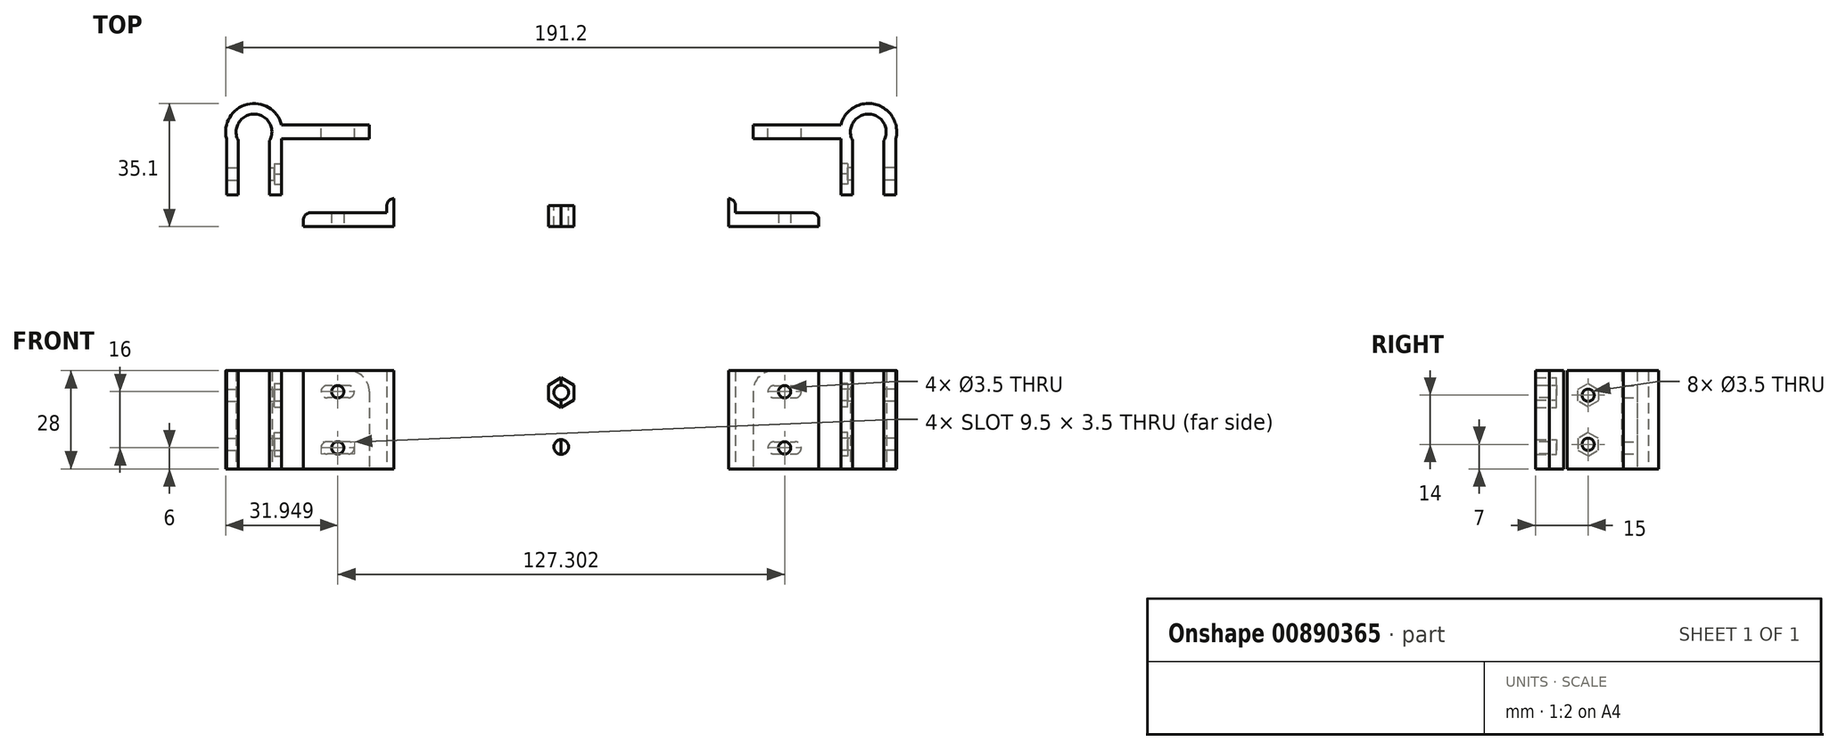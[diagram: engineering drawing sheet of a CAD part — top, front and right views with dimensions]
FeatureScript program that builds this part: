
annotation { "Feature Type Name" : "Feature", "Feature Type Description" : "" }
export const myFeature = defineFeature(function(context is Context, id is Id, definition is map)
    precondition{}
    {
        {
            var Q0;
            Q0=qCreatedBy(makeId("Top.planeOp"),FACE);
            var sketch = newSketch(context, id + "F0", { "sketchPlane" : qUnion([Q0])});
            skCircle(sketch, "E0", {"center": v(-87.5, 0) * mm, "radius": 5.1 * mm});
            skCircle(sketch, "E1", {"center": v(-87.5, 0) * mm, "radius": 8.1 * mm});
            skLineSegment(sketch, "E2.bottom", {"start": v(-95.35, -2) * mm, "end": v(-79.65, -2) * mm});
            skLineSegment(sketch, "E2.top", {"start": v(-95.35, -18) * mm, "end": v(-79.65, -18) * mm});
            skLineSegment(sketch, "E2.left", {"start": v(-95.35, -2) * mm, "end": v(-95.35, -18) * mm});
            skLineSegment(sketch, "E2.right", {"start": v(-79.65, -2) * mm, "end": v(-79.65, -18) * mm});
            skLineSegment(sketch, "E3.bottom", {"start": v(-91.95, -2.5) * mm, "end": v(-83.05, -2.5) * mm});
            skLineSegment(sketch, "E3.top", {"start": v(-91.95, -18) * mm, "end": v(-83.05, -18) * mm});
            skLineSegment(sketch, "E3.left", {"start": v(-91.95, -2.5) * mm, "end": v(-91.95, -18) * mm});
            skLineSegment(sketch, "E3.right", {"start": v(-83.05, -2.5) * mm, "end": v(-83.05, -18) * mm});
            skLineSegment(sketch, "E4.bottom", {"start": v(-79.65, 2) * mm, "end": v(-54.65, 2) * mm});
            skLineSegment(sketch, "E4.top", {"start": v(-79.65, -2) * mm, "end": v(-54.65, -2) * mm});
            skLineSegment(sketch, "E4.left", {"start": v(-79.65, 2) * mm, "end": v(-79.65, -2) * mm});
            skLineSegment(sketch, "E4.right", {"start": v(-54.65, 2) * mm, "end": v(-54.65, -2) * mm});
            skPoint(sketch, "E5", {"position": v(-54.65, 0) * mm});
            skSolve(sketch);
        }
        {
            var Q0;
            {var subQ0=sQuery(id+"F0.wireOp",EDGE,"E2.left");Q0=makeQuery(id+"F0.imprint","IMPRINT",FACE,{"disambiguationData":[TD([[makeQuery(id+"F0.imprint","IMPRINT",EDGE,{"derivedFrom":subQ0}),1.0]])]});}
            var Q1;
            {var subQ0=sQuery(id+"F0.wireOp",EDGE,"E2.bottom");var subQ1=sQuery(id+"F0.wireOp",EDGE,"E0");var subQ2=makeQuery(id+"F0.imprint","INTERSECT",VERTEX,{"disambiguationData":[OD(0.0)],"derivedFrom":[subQ1,subQ0]});Q1=makeQuery(id+"F0.imprint","IMPRINT",FACE,{"disambiguationData":[TD([[makeQuery(id+"F0.imprint","IMPRINT",EDGE,{"disambiguationData":[TD([[subQ2,-1.0]])],"derivedFrom":subQ1}),-1.0]])]});}
            var Q2;
            {var subQ0=sQuery(id+"F0.wireOp",EDGE,"E4.left");Q2=makeQuery(id+"F0.imprint","IMPRINT",FACE,{"disambiguationData":[TD([[makeQuery(id+"F0.imprint","IMPRINT",EDGE,{"derivedFrom":subQ0}),-1.0]])]});}
            var Q3;
            {var subQ0=sQuery(id+"F0.wireOp",EDGE,"E2.right");Q3=makeQuery(id+"F0.imprint","IMPRINT",FACE,{"disambiguationData":[TD([[makeQuery(id+"F0.imprint","IMPRINT",EDGE,{"derivedFrom":subQ0}),-1.0]])]});}
            var Q4;
            {var subQ1=sQuery(id+"F0.wireOp",EDGE,"E0");var subQ3=sQuery(id+"F0.wireOp",EDGE,"E2.bottom");var subQ4=makeQuery(id+"F0.imprint","INTERSECT",VERTEX,{"disambiguationData":[OD(1.0)],"derivedFrom":[subQ1,subQ3]});Q4=makeQuery(id+"F0.imprint","IMPRINT",FACE,{"disambiguationData":[TD([[makeQuery(id+"F0.imprint","IMPRINT",EDGE,{"disambiguationData":[TD([[subQ4,1.0]])],"derivedFrom":subQ1}),-1.0]])]});}
            var Q5;
            {var subQ0=sQuery(id+"F0.wireOp",EDGE,"E4.bottom");Q5=makeQuery(id+"F0.imprint","IMPRINT",FACE,{"disambiguationData":[TD([[makeQuery(id+"F0.imprint","IMPRINT",EDGE,{"derivedFrom":subQ0}),-1.0]])]});}
            var Q6;
            {var subQ0=sQuery(id+"F0.wireOp",EDGE,"E4.left");Q6=makeQuery(id+"F0.imprint","IMPRINT",FACE,{"disambiguationData":[TD([[makeQuery(id+"F0.imprint","IMPRINT",EDGE,{"derivedFrom":subQ0}),1.0]])]});}
            extrude(context, id + "F1", {"entities" : qUnion([Q0, Q1, Q2, Q3, Q4, Q5, Q6]), "depth" : 28 * mm, "offsetDistance" : 25 * mm});
        }
        {
            var Q0;
            Q0=makeQuery(id+"F1.opExtrude","SWEPT_FACE",FACE,{"disambiguationData":[OSD([sQuery(id+"F0.wireOp",EDGE,"E2.right")])]});
            var sketch = newSketch(context, id + "F2", { "sketchPlane" : qUnion([Q0])});
            skCircle(sketch, "E6", {"center": v(-12, 21) * mm, "radius": 1.75 * mm});
            skLineSegment(sketch, "E7", {"start": v(-2, 14) * mm, "end": v(-18, 14) * mm, "construction": true});
            skCircle(sketch, "E8.MirrorC", {"center": v(-12, 7) * mm, "radius": 1.75 * mm});
            skCircle(sketch, "E9.cCircle", {"center": v(-12, 21) * mm, "radius": 2.9 * mm, "construction": true});
            skLineSegment(sketch, "E9.0", {"start": v(-12, 17.65) * mm, "end": v(-14.9, 19.33) * mm});
            skLineSegment(sketch, "E9.1", {"start": v(-14.9, 19.33) * mm, "end": v(-14.9, 22.67) * mm});
            skLineSegment(sketch, "E9.2", {"start": v(-14.9, 22.67) * mm, "end": v(-12, 24.35) * mm});
            skLineSegment(sketch, "E9.3", {"start": v(-12, 24.35) * mm, "end": v(-9.1, 22.67) * mm});
            skLineSegment(sketch, "E9.4", {"start": v(-9.1, 22.67) * mm, "end": v(-9.1, 19.33) * mm});
            skLineSegment(sketch, "E9.5", {"start": v(-9.1, 19.33) * mm, "end": v(-12, 17.65) * mm});
            skPoint(sketch, "E9.0.midPoint", {"position": v(-13.45, 18.49) * mm});
            skLineSegment(sketch, "E10.MirrorCS", {"start": v(-12, 10.35) * mm, "end": v(-14.9, 8.67) * mm});
            skLineSegment(sketch, "E11.MirrorCS", {"start": v(-9.1, 8.67) * mm, "end": v(-12, 10.35) * mm});
            skLineSegment(sketch, "E12.MirrorCS", {"start": v(-9.1, 5.33) * mm, "end": v(-9.1, 8.67) * mm});
            skLineSegment(sketch, "E13.MirrorCS", {"start": v(-12, 3.65) * mm, "end": v(-9.1, 5.33) * mm});
            skLineSegment(sketch, "E14.MirrorCS", {"start": v(-14.9, 5.33) * mm, "end": v(-12, 3.65) * mm});
            skLineSegment(sketch, "E15.MirrorCS", {"start": v(-14.9, 8.67) * mm, "end": v(-14.9, 5.33) * mm});
            skSolve(sketch);
        }
        {
            var Q0;
            Q0=makeQuery(id+"F1.opExtrude","SWEPT_FACE",FACE,{"disambiguationData":[OSD([sQuery(id+"F0.wireOp",EDGE,"E4.bottom")])]});
            var sketch = newSketch(context, id + "F3", { "sketchPlane" : qUnion([Q0])});
            skLineSegment(sketch, "E16", {"start": v(54.65, 14) * mm, "end": v(79.65, 14) * mm, "construction": true});
            skLineSegment(sketch, "E17", {"start": v(60.65, 22) * mm, "end": v(66.65, 22) * mm, "construction": true});
            skArc(sketch, "E18.0.startCap", {"start": v(60.65, 20.25) * mm, "mid": v(58.9, 22) * mm, "end": v(60.65, 23.75) * mm});
            skArc(sketch, "E18.0.endCap", {"start": v(66.65, 23.75) * mm, "mid": v(68.4, 22) * mm, "end": v(66.65, 20.25) * mm});
            skLineSegment(sketch, "E18.0.left", {"start": v(60.65, 23.75) * mm, "end": v(66.65, 23.75) * mm});
            skLineSegment(sketch, "E18.0.right", {"start": v(60.65, 20.25) * mm, "end": v(66.65, 20.25) * mm});
            skLineSegment(sketch, "E19.MirrorCS", {"start": v(60.65, 4.25) * mm, "end": v(66.65, 4.25) * mm});
            skArc(sketch, "E20.MirrorCS", {"start": v(66.65, 4.25) * mm, "mid": v(68.4, 6) * mm, "end": v(66.65, 7.75) * mm});
            skLineSegment(sketch, "E21.MirrorCS", {"start": v(60.65, 6) * mm, "end": v(66.65, 6) * mm, "construction": true});
            skLineSegment(sketch, "E22.MirrorCS", {"start": v(60.65, 7.75) * mm, "end": v(66.65, 7.75) * mm});
            skArc(sketch, "E23.MirrorCS", {"start": v(60.65, 7.75) * mm, "mid": v(58.9, 6) * mm, "end": v(60.65, 4.25) * mm});
            skSolve(sketch);
        }
        {
            var Q0;
            Q0 = qSketchRegion(id + "F2", true);
            extrude(context, id + "F4", {"entities" : qUnion([Q0]), "operationType" : NewBodyOperationType.REMOVE, "oppositeDirection" : true, "depth" : 2 * mm, "offsetDistance" : 25 * mm});
        }
        {
            var Q0;
            Q0=makeQuery(id+"F4.boolean.opBoolean","SPLIT",FACE,{"disambiguationData":[TD([makeQuery(id+"F4.opExtrude","SWEPT_FACE",FACE,{"disambiguationData":[OSD([sQuery(id+"F2.wireOp",EDGE,"E6")])]})])],"derivedFrom":makeQuery(id+"F1.opExtrude","SWEPT_FACE",FACE,{"disambiguationData":[OSD([sQuery(id+"F0.wireOp",EDGE,"E2.right")])]})});
            var Q1;
            Q1=makeQuery(id+"F4.boolean.opBoolean","SPLIT",FACE,{"disambiguationData":[TD([makeQuery(id+"F4.opExtrude","SWEPT_FACE",FACE,{"disambiguationData":[OSD([sQuery(id+"F2.wireOp",EDGE,"E8.MirrorC")])]})])],"derivedFrom":makeQuery(id+"F1.opExtrude","SWEPT_FACE",FACE,{"disambiguationData":[OSD([sQuery(id+"F0.wireOp",EDGE,"E2.right")])]})});
            extrude(context, id + "F5", {"entities" : qUnion([Q0, Q1]), "operationType" : NewBodyOperationType.REMOVE, "oppositeDirection" : true, "depth" : 25 * mm, "offsetDistance" : 25 * mm});
        }
        {
            var Q0;
            Q0 = qSketchRegion(id + "F3", true);
            extrude(context, id + "F6", {"entities" : qUnion([Q0]), "operationType" : NewBodyOperationType.REMOVE, "oppositeDirection" : true, "depth" : 25 * mm, "offsetDistance" : 25 * mm});
        }
        {
            var Q0;
            Q0=makeQuery(id+"F1.opExtrude","CAP_EDGE",EDGE,{"disambiguationData":[OSD([sQuery(id+"F0.wireOp",EDGE,"E4.right")])],"isStart":false});
            fillet(context, id + "F7", {"entities" : qUnion([Q0]), "tangentPropagation" : true, "radius" : 6 * mm, "defaultsChanged" : true, "vertexSettings" : [], "allowEdgeOverflow" : false});
        }
        {
            var Q0;
            Q0=makeQuery(id+"F1.opExtrude","SWEPT_BODY",BODY,{"disambiguationData":[OSD([sQuery(id+"F0.wireOp",EDGE,"E0"),sQuery(id+"F0.wireOp",EDGE,"E1"),sQuery(id+"F0.wireOp",EDGE,"E2.top"),sQuery(id+"F0.wireOp",EDGE,"E2.left"),sQuery(id+"F0.wireOp",EDGE,"E2.right"),sQuery(id+"F0.wireOp",EDGE,"E3.left"),sQuery(id+"F0.wireOp",EDGE,"E3.right"),sQuery(id+"F0.wireOp",EDGE,"E4.bottom"),sQuery(id+"F0.wireOp",EDGE,"E4.top"),sQuery(id+"F0.wireOp",EDGE,"E4.right")])]});
            var Q1;
            Q1=qCreatedBy(makeId("Right.planeOp"),FACE);
            mirror(context, id + "F8", {"entities" : qUnion([Q0]), "mirrorPlane" : qUnion([Q1])});
        }
        {
            var Q0;
            Q0=makeQuery(id+"F1.opExtrude","SWEPT_FACE",FACE,{"disambiguationData":[OSD([sQuery(id+"F0.wireOp",EDGE,"E4.top")])]});
            cPlane(context, id + "F9", {"entities" : qUnion([Q0]), "cplaneType" : CPlaneType.OFFSET, "offset" : 25 * mm, "width" : 150 * mm, "height" : 150 * mm});
        }
        {
            var Q0;
            Q0=qCreatedBy(id+"F9.planeOp",FACE);
            var sketch = newSketch(context, id + "F10", { "sketchPlane" : qUnion([Q0])});
            skLineSegment(sketch, "E24.bottom", {"start": v(-73.4, 28) * mm, "end": v(0, 28) * mm});
            skLineSegment(sketch, "E24.top", {"start": v(-73.4, 0) * mm, "end": v(0, 0) * mm});
            skLineSegment(sketch, "E24.left", {"start": v(-73.4, 28) * mm, "end": v(-73.4, 0) * mm});
            skLineSegment(sketch, "E24.right", {"start": v(0, 28) * mm, "end": v(0, 0) * mm});
            skCircle(sketch, "E25", {"center": v(-63.65, 22) * mm, "radius": 1.75 * mm});
            skLineSegment(sketch, "E26", {"start": v(-73.4, 14) * mm, "end": v(0, 14) * mm, "construction": true});
            skLineSegment(sketch, "E27", {"start": v(-63.65, 23.75) * mm, "end": v(-63.65, 20.25) * mm, "construction": true});
            skCircle(sketch, "E28.MirrorC", {"center": v(-63.65, 6) * mm, "radius": 1.75 * mm});
            skLineSegment(sketch, "E29", {"start": v(-49.65, 28) * mm, "end": v(-49.65, 0) * mm});
            skSolve(sketch);
        }
        {
            var Q0;
            {var subQ0=sQuery(id+"F10.wireOp",EDGE,"E24.left");Q0=makeQuery(id+"F10.imprint","IMPRINT",FACE,{"disambiguationData":[TD([[makeQuery(id+"F10.imprint","IMPRINT",EDGE,{"derivedFrom":subQ0}),1.0]])]});}
            extrude(context, id + "F11", {"entities" : qUnion([Q0]), "oppositeDirection" : true, "depth" : 4 * mm, "offsetDistance" : 25 * mm});
        }
        {
            var Q0;
            {var subQ2=sQuery(id+"F10.wireOp",EDGE,"E24.right");Q0=makeQuery(id+"F10.imprint","IMPRINT",FACE,{"disambiguationData":[TD([[makeQuery(id+"F10.imprint","IMPRINT",EDGE,{"derivedFrom":subQ2}),-1.0]])]});}
            extrude(context, id + "F12", {"entities" : qUnion([Q0]), "operationType" : NewBodyOperationType.ADD, "oppositeDirection" : true, "depth" : 8 * mm, "offsetDistance" : 25 * mm});
        }
        {
            var Q0;
            Q0=makeQuery(id+"F11.opExtrude","CAP_EDGE",EDGE,{"disambiguationData":[OSD([sQuery(id+"F10.wireOp",EDGE,"E24.left")])],"isStart":false});
            var Q1;
            Q1=makeQuery(id+"F12.opExtrude","CAP_EDGE",EDGE,{"disambiguationData":[OSD([sQuery(id+"F10.wireOp",EDGE,"E29")])],"isStart":false});
            var Q2;
            Q2=makeQuery(id+"F11.opExtrude","CAP_EDGE",EDGE,{"disambiguationData":[OSD([sQuery(id+"F10.wireOp",EDGE,"E29")])],"isStart":false});
            fillet(context, id + "F13", {"entities" : qUnion([Q0, Q1, Q2]), "tangentPropagation" : true, "radius" : 2 * mm, "defaultsChanged" : false, "vertexSettings" : [], "allowEdgeOverflow" : false});
        }
        {
            var Q0;
            Q0=makeQuery(id+"F11.opExtrude","SWEPT_BODY",BODY,{"disambiguationData":[OSD([sQuery(id+"F10.wireOp",EDGE,"E24.bottom"),sQuery(id+"F10.wireOp",EDGE,"E24.top"),sQuery(id+"F10.wireOp",EDGE,"E24.left"),sQuery(id+"F10.wireOp",EDGE,"E25"),sQuery(id+"F10.wireOp",EDGE,"E28.MirrorC"),sQuery(id+"F10.wireOp",EDGE,"E29")])]});
            var Q1;
            Q1=qCreatedBy(makeId("Right.planeOp"),FACE);
            mirror(context, id + "F14", {"operationType" : NewBodyOperationType.ADD, "entities" : qUnion([Q0]), "mirrorPlane" : qUnion([Q1])});
        }
        {
            var Q0;
            {var subQ0=makeQuery(id+"F12.opExtrude","CAP_FACE",FACE,{"disambiguationData":[OSD([sQuery(id+"F10.wireOp",EDGE,"E24.bottom"),sQuery(id+"F10.wireOp",EDGE,"E24.top"),sQuery(id+"F10.wireOp",EDGE,"E24.right"),sQuery(id+"F10.wireOp",EDGE,"E29")])],"isStart":false});Q0=makeQuery(id+"F14.boolean.opBoolean","MERGE",FACE,{"derivedFrom":[subQ0,makeQuery(id+"F14.opPattern","COPY",FACE,{"derivedFrom":subQ0,"instanceName":"1"})]});}
            var sketch = newSketch(context, id + "F15", { "sketchPlane" : qUnion([Q0])});
            skCircle(sketch, "E30", {"center": v(0, 21.75) * mm, "radius": 2.1 * mm});
            skLineSegment(sketch, "E31", {"start": v(0, 28) * mm, "end": v(0, 0) * mm, "construction": true});
            skPoint(sketch, "E32", {"position": v(0, 14) * mm});
            skLineSegment(sketch, "E33", {"start": v(-47.65, 14) * mm, "end": v(47.65, 14) * mm, "construction": true});
            skCircle(sketch, "E34.MirrorC", {"center": v(0, 6.25) * mm, "radius": 2.1 * mm});
            skCircle(sketch, "E35.cCircle", {"center": v(0, 21.75) * mm, "radius": 3.65 * mm, "construction": true});
            skLineSegment(sketch, "E35.0", {"start": v(0, 17.54) * mm, "end": v(-3.65, 19.64) * mm});
            skLineSegment(sketch, "E35.1", {"start": v(-3.65, 19.64) * mm, "end": v(-3.65, 23.86) * mm});
            skLineSegment(sketch, "E35.2", {"start": v(-3.65, 23.86) * mm, "end": v(0, 25.96) * mm});
            skLineSegment(sketch, "E35.3", {"start": v(0, 25.96) * mm, "end": v(3.65, 23.86) * mm});
            skLineSegment(sketch, "E35.4", {"start": v(3.65, 23.86) * mm, "end": v(3.65, 19.64) * mm});
            skLineSegment(sketch, "E35.5", {"start": v(3.65, 19.64) * mm, "end": v(0, 17.54) * mm});
            skPoint(sketch, "E35.0.midPoint", {"position": v(-1.83, 18.59) * mm});
            skLineSegment(sketch, "E36.MirrorCS", {"start": v(0, 10.46) * mm, "end": v(-3.65, 8.36) * mm});
            skLineSegment(sketch, "E37.MirrorCS", {"start": v(3.65, 8.36) * mm, "end": v(0, 10.46) * mm});
            skLineSegment(sketch, "E38.MirrorCS", {"start": v(3.65, 4.14) * mm, "end": v(3.65, 8.36) * mm});
            skLineSegment(sketch, "E39.MirrorCS", {"start": v(0, 2.04) * mm, "end": v(3.65, 4.14) * mm});
            skLineSegment(sketch, "E40.MirrorCS", {"start": v(-3.65, 4.14) * mm, "end": v(0, 2.04) * mm});
            skLineSegment(sketch, "E41.MirrorCS", {"start": v(-3.65, 8.36) * mm, "end": v(-3.65, 4.14) * mm});
            skSolve(sketch);
        }
        {
            var Q0;
            Q0=makeQuery(id+"F15.imprint","IMPRINT",FACE,{"disambiguationData":[TD([[makeQuery(id+"F15.imprint","IMPRINT",EDGE,{"derivedFrom":sQuery(id+"F15.wireOp",EDGE,"E34.MirrorC")}),1.0]])]});
            var Q1;
            Q1=makeQuery(id+"F15.imprint","IMPRINT",FACE,{"disambiguationData":[TD([[makeQuery(id+"F15.imprint","IMPRINT",EDGE,{"derivedFrom":sQuery(id+"F15.wireOp",EDGE,"E30")}),-1.0]])]});
            extrude(context, id + "F16", {"entities" : qUnion([Q0, Q1]), "operationType" : NewBodyOperationType.REMOVE, "oppositeDirection" : true, "depth" : 2 * mm, "offsetDistance" : 25 * mm});
        }
        {
            var Q0;
            {var subQ0=makeQuery(id+"F12.opExtrude","CAP_FACE",FACE,{"disambiguationData":[OSD([sQuery(id+"F10.wireOp",EDGE,"E24.bottom"),sQuery(id+"F10.wireOp",EDGE,"E24.top"),sQuery(id+"F10.wireOp",EDGE,"E24.right"),sQuery(id+"F10.wireOp",EDGE,"E29")])],"isStart":false});Q0=makeQuery(id+"F16.boolean.opBoolean","SPLIT",FACE,{"disambiguationData":[TD([makeQuery(id+"F16.opExtrude","SWEPT_FACE",FACE,{"disambiguationData":[OSD([sQuery(id+"F15.wireOp",EDGE,"E30")])]})])],"derivedFrom":makeQuery(id+"F14.boolean.opBoolean","MERGE",FACE,{"derivedFrom":[subQ0,makeQuery(id+"F14.opPattern","COPY",FACE,{"derivedFrom":subQ0,"instanceName":"1"})]})});}
            var Q1;
            {var subQ0=makeQuery(id+"F12.opExtrude","CAP_FACE",FACE,{"disambiguationData":[OSD([sQuery(id+"F10.wireOp",EDGE,"E24.bottom"),sQuery(id+"F10.wireOp",EDGE,"E24.top"),sQuery(id+"F10.wireOp",EDGE,"E24.right"),sQuery(id+"F10.wireOp",EDGE,"E29")])],"isStart":false});Q1=makeQuery(id+"F16.boolean.opBoolean","SPLIT",FACE,{"disambiguationData":[TD([makeQuery(id+"F16.opExtrude","SWEPT_FACE",FACE,{"disambiguationData":[OSD([sQuery(id+"F15.wireOp",EDGE,"E34.MirrorC")])]})])],"derivedFrom":makeQuery(id+"F14.boolean.opBoolean","MERGE",FACE,{"derivedFrom":[subQ0,makeQuery(id+"F14.opPattern","COPY",FACE,{"derivedFrom":subQ0,"instanceName":"1"})]})});}
            extrude(context, id + "F17", {"entities" : qUnion([Q0, Q1]), "operationType" : NewBodyOperationType.REMOVE, "oppositeDirection" : true, "depth" : 25 * mm, "offsetDistance" : 25 * mm});
        }
    });
